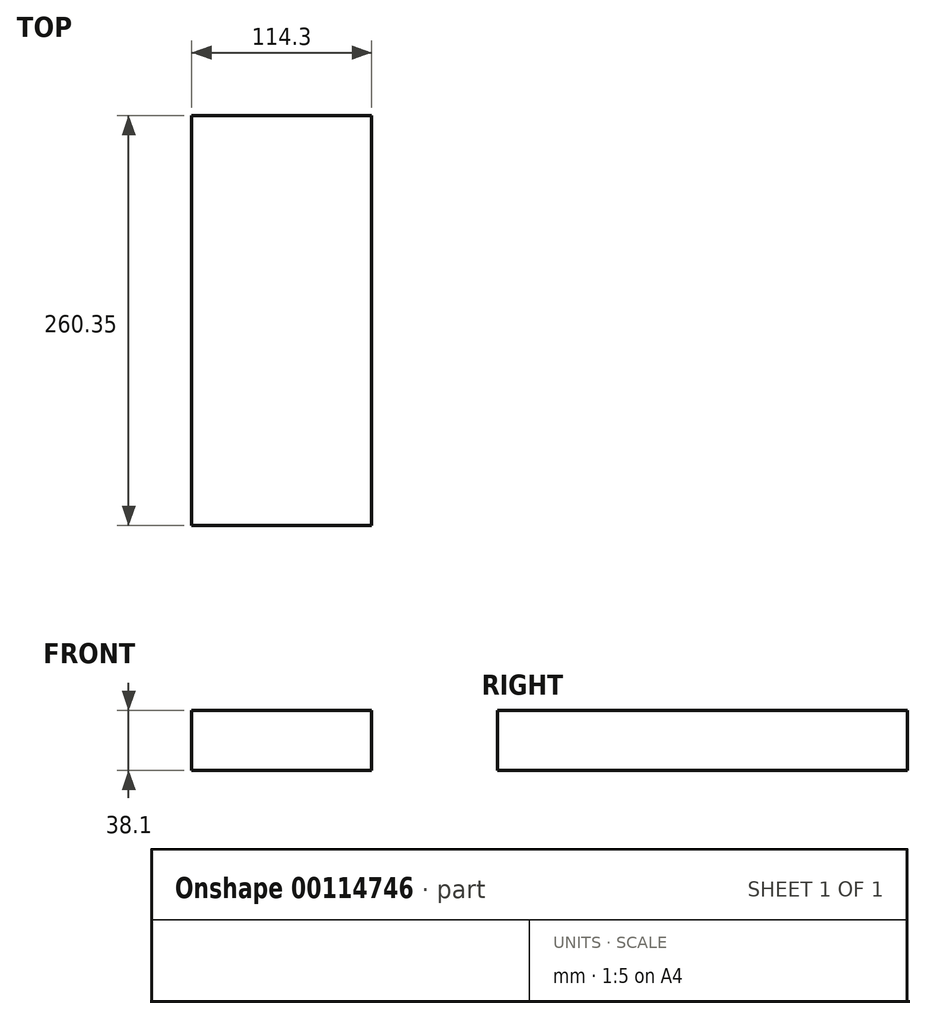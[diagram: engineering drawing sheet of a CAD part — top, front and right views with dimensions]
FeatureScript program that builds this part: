
annotation { "Feature Type Name" : "Feature", "Feature Type Description" : "" }
export const myFeature = defineFeature(function(context is Context, id is Id, definition is map)
    precondition{}
    {
        {
            var Q0;
            Q0=qCreatedBy(makeId("Top.planeOp"),FACE);
            var sketch = newSketch(context, id + "F0", { "sketchPlane" : qUnion([Q0])});
            skLineSegment(sketch, "E0.bottom", {"start": v(0, 0) * mm, "end": v(114.3, 0) * mm});
            skLineSegment(sketch, "E0.top", {"start": v(0, 260.35) * mm, "end": v(114.3, 260.35) * mm});
            skLineSegment(sketch, "E0.left", {"start": v(0, 0) * mm, "end": v(0, 260.35) * mm});
            skLineSegment(sketch, "E0.right", {"start": v(114.3, 0) * mm, "end": v(114.3, 260.35) * mm});
            skSolve(sketch);
        }
        {
            var Q0;
            Q0 = qSketchRegion(id + "F0", true);
            extrude(context, id + "F1", {"entities" : qUnion([Q0]), "depth" : 38.1 * mm});
        }
    });
